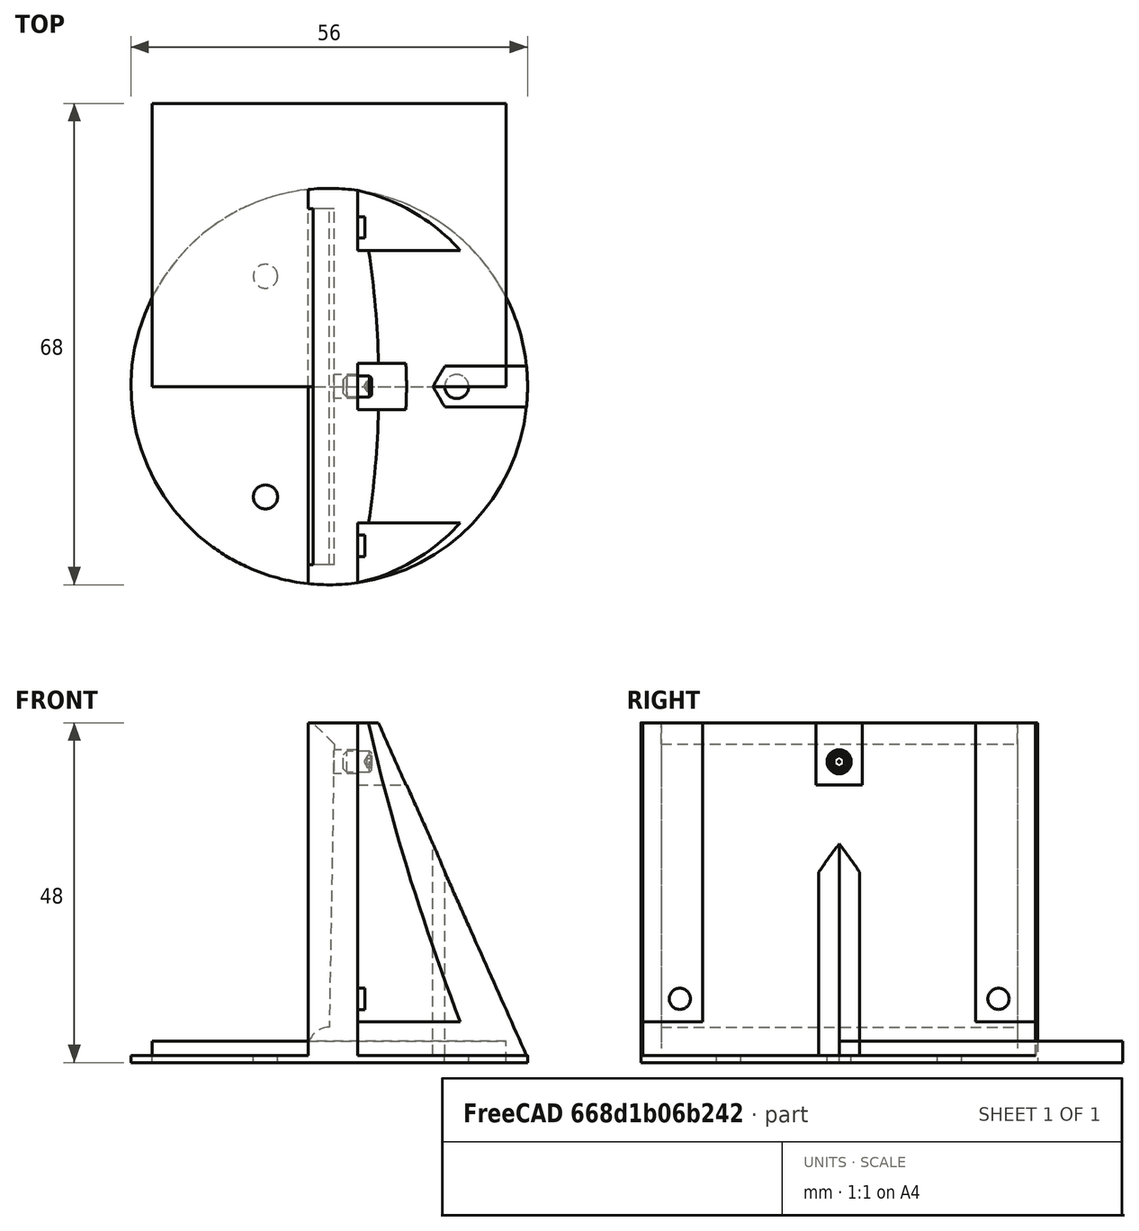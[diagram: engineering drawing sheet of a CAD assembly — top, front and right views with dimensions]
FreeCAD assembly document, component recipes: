
FREECAD ASSEMBLY — COMPONENT RECIPES ("IndexMirror")

This assembly document has 2 components, labeled P0..P1 below (a component is one placed body or linked part). 2 of them carry a construction recipe — the FreeCAD feature program that regenerates the part from scratch, quoted from this document or its linked companion documents; the rest are supplied as boundary geometry only. No exploded tour is included for this assembly.
COMPONENT P0 — recipe-attached ("IndexMirrorFrame", modeled in this document).
Construction recipe (the document's own serialized feature program — sketch geometry with constraints, then the solid features built on it; lengths are millimeters unless a unit is written):

FEATURE [PartDesign::Plane] DatumPlane  label="Plane_Base"
  AttachmentSupport = -> [XY_Plane001]
  Length = 60
  MapMode = 5
  ResizeMode = 0
  Width = 60
FEATURE [Sketcher::SketchObject] Sketch  label="Sketch_Base"
  ArcFitTolerance = 0
  AttachmentSupport = -> [DatumPlane]
  FullyConstrained = true
  MakeInternals = false
  MapMode = 5
  expr: Constraints[0] = <<Dimensions>>.index_mirror_base_diameter
  sketch-geometry (1):
    g0: Circle CenterX=0 CenterY=0 CenterZ=0 NormalX=0 NormalY=0 NormalZ=1 AngleXU=0 Radius=28
  constraints (2):
    c: Diameter(g0) = 56
    c: Coincident(g-1,g0)
FEATURE [PartDesign::Plane] DatumPlane001  label="Plane_BaseTop"
  AttachmentOffset = pos=(0,0,1) rot=(0,0,1;0rad)
  AttachmentSupport = -> [DatumPlane]
  Length = 60
  MapMode = 5
  Placement = pos=(0,0,1) rot=(0,0,1;0rad)
  ResizeMode = 0
  Width = 60
  expr: .AttachmentOffset.Base.z = <<Dimensions>>.index_mirror_base_thickness
FEATURE [PartDesign::Plane] DatumPlane002  label="Plane_MirrorBack"
  AttachmentSupport = -> [YZ_Plane002]
  Length = 60
  MapMode = 5
  Placement = pos=(0,0,0) rot=(0.57735,0.57735,0.57735;2.0944rad)
  ResizeMode = 0
  Width = 60
FEATURE [PartDesign::Plane] DatumPlane004  label="Plane_FrameFront"
  AttachmentOffset = pos=(0,0,-3) rot=(0,0,1;0rad)
  AttachmentSupport = -> [DatumPlane002]
  Length = 60
  MapMode = 5
  Placement = pos=(-3,0,0) rot=(0.57735,0.57735,0.57735;2.0944rad)
  ResizeMode = 0
  Width = 60
  expr: .AttachmentOffset.Base.z = -<<Dimensions>>.index_mirror_mirror_thickness
FEATURE [PartDesign::Plane] DatumPlane003  label="Plane_FrameBack"
  AttachmentOffset = pos=(0,0,7) rot=(0,0,1;0rad)
  AttachmentSupport = -> [DatumPlane004]
  Length = 60
  MapMode = 5
  Placement = pos=(4,0,0) rot=(0.57735,0.57735,0.57735;2.0944rad)
  ResizeMode = 0
  Width = 60
  expr: .AttachmentOffset.Base.z = <<Dimensions>>.mirror_frame_thickness
FEATURE [PartDesign::Plane] DatumPlane005  label="Plane_Top"
  AttachmentOffset = pos=(0,0,48) rot=(0,0,1;0rad)
  AttachmentSupport = -> [XY_Plane002]
  Length = 60
  MapMode = 5
  Placement = pos=(0,0,48) rot=(0,0,1;0rad)
  ResizeMode = 0
  Width = 60
  expr: .AttachmentOffset.Base.z = <<Dimensions>>.index_mirror_mirror_offset + <<Dimensions>>.index_mirror_mirror_height + <<Dimensions>>.mirror_frame_width
FEATURE [Sketcher::SketchObject] Sketch003
  ArcFitTolerance = 0
  AttachmentSupport = -> [DatumPlane001]
  FullyConstrained = true
  MakeInternals = false
  MapMode = 5
  Placement = pos=(0,0,1) rot=(0,0,1;0rad)
  expr: Constraints[4] = <<Dimensions>>.index_mirror_screw_diameter
  sketch-geometry (8):
    g0: Circle CenterX=-10.6066 CenterY=10.6066 CenterZ=0 NormalX=0 NormalY=0 NormalZ=1 AngleXU=0 Radius=1.5
    g1: Circle CenterX=-10.6066 CenterY=-10.6066 CenterZ=0 NormalX=0 NormalY=0 NormalZ=1 AngleXU=0 Radius=1.5
    g2: Circle CenterX=10.6066 CenterY=-10.6066 CenterZ=0 NormalX=0 NormalY=0 NormalZ=1 AngleXU=0 Radius=1.5
    g3: Circle CenterX=10.6066 CenterY=10.6066 CenterZ=0 NormalX=0 NormalY=0 NormalZ=1 AngleXU=0 Radius=1.5
    g4: LineSegment [constr] StartX=-10.6066 StartY=10.6066 StartZ=0 EndX=-10.6066 EndY=-10.6066 EndZ=0
    g5: LineSegment [constr] StartX=-10.6066 StartY=10.6066 StartZ=0 EndX=10.6066 EndY=10.6066 EndZ=0
    g6: LineSegment [constr] StartX=-10.6066 StartY=-10.6066 StartZ=0 EndX=10.6066 EndY=-10.6066 EndZ=0
    g7: LineSegment [constr] StartX=10.6066 StartY=10.6066 StartZ=0 EndX=10.6066 EndY=-10.6066 EndZ=0
  constraints (19):
    c: Equal(g0,g3)
    c: Equal(g1,g2)
    c: Equal(g0,g1)
    c: Distance(g0,g-1) = 15
    c: Diameter(g0) = 3
    c: Symmetric(g0,g2,g-1)
    c: Coincident(g4,g0)
    c: Coincident(g4,g1)
    c: Vertical(g4)
    c: Coincident(g5,g0)
    c: Coincident(g5,g3)
    c: Horizontal(g5)
    c: Coincident(g6,g1)
    c: Horizontal(g6)
    c: Coincident(g2,g6)
    c: Coincident(g7,g3)
    c: Coincident(g7,g2)
    c: Vertical(g7)
    c: Equal(g4,g6)
FEATURE [PartDesign::Line] HoleAxis_002  label="HoleAxis_1"
  AttacherType = Attacher::AttachEngineLine
  AttachmentOffset = pos=(0,0,1) rot=(0,0,1;0rad)
  AttachmentSupport = -> [Sketch003]
  Length = 4.2272
  MapMode = 19
  Placement = pos=(10.6066,10.6066,2) rot=(0,0,1;0rad)
  ResizeMode = 1
  expr: .AttachmentOffset.Base.z = <<Dimensions>>.index_mirror_base_thickness
FEATURE [PartDesign::Pad] Pad  label="Pad_Base"
  Direction = (0,0,1)
  Length = 10
  Length2 = 10
  Profile = -> Sketch
  ReferenceAxis = -> Sketch [N_Axis]
  Suppressed = false
  Type = 3
  UpToFace = -> DatumPlane001
FEATURE [Sketcher::SketchObject] Sketch010  label="Sketch_LoftBottom"
  ArcFitTolerance = 0
  AttachmentSupport = -> [DatumPlane001]
  ExternalGeometry = -> [Sketch,DatumPlane004]
  FullyConstrained = true
  MakeInternals = false
  MapMode = 5
  Placement = pos=(0,0,1) rot=(0,0,1;0rad)
  expr: Constraints[7] = <<Dimensions>>.mirror_frame_thickness
  sketch-geometry (4):
    g0: LineSegment StartX=-3 StartY=-27.8388 StartZ=0 EndX=-3 EndY=27.8388 EndZ=0
    g1: ArcOfCircle CenterX=0 CenterY=0 CenterZ=0 NormalX=0 NormalY=0 NormalZ=1 AngleXU=0 Radius=28 StartAngle=4.85574 EndAngle=7.71063
    g2: ArcOfCircle CenterX=0 CenterY=0 CenterZ=0 NormalX=0 NormalY=0 NormalZ=1 AngleXU=0 Radius=28 StartAngle=1.42745 EndAngle=1.67815
    g3: ArcOfCircle CenterX=0 CenterY=0 CenterZ=0 NormalX=0 NormalY=0 NormalZ=1 AngleXU=0 Radius=28 StartAngle=4.60504 EndAngle=4.85574
  constraints (12):
    c: PointOnObject(g0,g-4)
    c: Vertical(g0)
    c: Coincident(g2,g1)
    c: Coincident(g3,g1)
    c: Coincident(g3,g1)
    c: Coincident(g2,g1)
    c: Coincident(g2,g0)
    c: DistanceX(g0,g1) = 7
    c: Coincident(g3,g0)
    c: Coincident(g1,g-3)
    c: Equal(g1,g-3)
    c: Vertical(g1,g1)
FEATURE [Sketcher::SketchObject] Sketch011  label="Sketch_LoftTop"
  ArcFitTolerance = 0
  AttachmentSupport = -> [DatumPlane005]
  ExternalGeometry = -> [Sketch,DatumPlane004]
  FullyConstrained = true
  MakeInternals = false
  MapMode = 5
  Placement = pos=(0,0,48) rot=(0,0,1;0rad)
  expr: Constraints[11] = <<Dimensions>>.mirror_frame_thickness
  sketch-geometry (6):
    g0: LineSegment StartX=-3 StartY=27.8388 StartZ=0 EndX=-3 EndY=-27.8388 EndZ=0
    g1: LineSegment [constr] StartX=0 StartY=0 StartZ=0 EndX=-3 EndY=0 EndZ=0
    g2: ArcOfCircle CenterX=-122.5 CenterY=4.05e-14 CenterZ=0 NormalX=0 NormalY=0 NormalZ=1 AngleXU=0 Radius=129.5 StartAngle=6.06752 EndAngle=6.49885
    g3: ArcOfCircle CenterX=0 CenterY=0 CenterZ=0 NormalX=0 NormalY=0 NormalZ=1 AngleXU=0 Radius=28 StartAngle=1.42745 EndAngle=1.67815
    g4: ArcOfCircle CenterX=0 CenterY=0 CenterZ=0 NormalX=0 NormalY=0 NormalZ=1 AngleXU=0 Radius=28 StartAngle=4.60504 EndAngle=4.85574
    g5: GeomPoint [constr] X=7 Y=0 Z=0
  constraints (17):
    c: PointOnObject(g1,g0)
    c: Horizontal(g1)
    c: Symmetric(g0,g0,g1)
    c: PointOnObject(g0,g-4)
    c: Coincident(g-3,g1)
    c: Coincident(g3,g2)
    c: Coincident(g4,g2)
    c: Coincident(g3,g4)
    c: PointOnObject(g5,g2)
    c: Horizontal(g5,g1)
    c: DistanceX(g1,g5) = 10
    c: DistanceX(g0,g2) = 7
    c: Coincident(g0,g3)
    c: Coincident(g1,g3)
    c: Equal(g3,g-3)
    c: Vertical(g2,g2)
    c: Coincident(g0,g4)
FEATURE [PartDesign::AdditiveLoft] AdditiveLoft
  BaseFeature = -> Pad
  Closed = false
  Profile = -> Sketch010
  Ruled = false
  Sections = -> [Sketch011]
  Suppressed = false
FEATURE [Sketcher::SketchObject] Sketch012  label="Sketch_MirrorSlot"
  ArcFitTolerance = 0
  AttachmentSupport = -> [XZ_Plane002]
  ExternalGeometry = -> [DatumPlane002,DatumPlane004]
  FullyConstrained = true
  MakeInternals = false
  MapMode = 5
  Placement = pos=(0,0,0) rot=(1,0,0;1.5708rad)
  expr: Constraints[7] = <<Dimensions>>.index_mirror_mirror_offset
  expr: Constraints[8] = <<Dimensions>>.index_mirror_mirror_height
  sketch-geometry (4):
    g0: LineSegment StartX=0.698203 StartY=45 StartZ=0 EndX=-1e-15 EndY=5 EndZ=0
    g1: LineSegment StartX=0.698203 StartY=45 StartZ=0 EndX=-3 EndY=48.6982 EndZ=0
    g2: ArcOfCircle CenterX=-1e-15 CenterY=2 CenterZ=0 NormalX=0 NormalY=0 NormalZ=1 AngleXU=0 Radius=3 StartAngle=1.5708 EndAngle=3.14159
    g3: LineSegment StartX=-3 StartY=48.6982 StartZ=0 EndX=-3 EndY=2 EndZ=0
  constraints (13):
    c: Coincident(g1,g0)
    c: Coincident(g2,g0)
    c: Coincident(g3,g1)
    c: Coincident(g3,g2)
    c: PointOnObject(g2,g-4)
    c: Horizontal(g2,g2)
    c: Vertical(g2,g0)
    c: DistanceY(g-1,g0) = 5
    c: DistanceY(g0,g0) = 40
    c: Angle(g3,g1) = 0.785398
    c: PointOnObject(g0,g-3)
    c: PointOnObject(g1,g-4)
    c: Angle(g-3,g0) = 3.12414
FEATURE [PartDesign::Pocket] Pocket  label="Pocket_MirrorSlot"
  BaseFeature = -> AdditiveLoft
  Direction = (0,1,-2e-16)
  Length = 50.3
  Length2 = 5
  Midplane = true
  Profile = -> Sketch012
  ReferenceAxis = -> Sketch012 [N_Axis]
  Suppressed = false
  Type = 0
  expr: Length = <<Dimensions>>.index_mirror_mirror_width + 2 * <<Dimensions>>.clearance_tight_fit
FEATURE [Sketcher::SketchObject] Sketch013  label="Sketch_Screw"
  ArcFitTolerance = 0
  AttachmentSupport = -> [DatumPlane]
  ExternalGeometry = -> [Sketch]
  FullyConstrained = true
  MakeInternals = false
  MapMode = 5
  expr: Constraints[17] = <<Dimensions>>.index_mirror_screw_diameter
  expr: Constraints[18] = <<Dimensions>>.index_mirror_nut_S
  expr: Constraints[25] = <<Dimensions>>.index_mirror_screw_center_distance
  sketch-geometry (9):
    g0: Circle CenterX=-9 CenterY=15.5885 CenterZ=0 NormalX=0 NormalY=0 NormalZ=1 AngleXU=0 Radius=1.5
    g1: LineSegment [constr] StartX=-7.41229 StartY=12.8385 StartZ=0 EndX=-5.82457 EndY=15.5885 EndZ=0
    g2: LineSegment [constr] StartX=-5.82457 StartY=15.5885 StartZ=0 EndX=-7.41229 EndY=18.3385 EndZ=0
    g3: LineSegment [constr] StartX=-7.41229 StartY=18.3385 StartZ=0 EndX=-10.5877 EndY=18.3385 EndZ=0
    g4: LineSegment [constr] StartX=-10.5877 StartY=18.3385 StartZ=0 EndX=-12.1754 EndY=15.5885 EndZ=0
    g5: LineSegment [constr] StartX=-12.1754 StartY=15.5885 StartZ=0 EndX=-10.5877 EndY=12.8385 EndZ=0
    g6: LineSegment [constr] StartX=-10.5877 StartY=12.8385 StartZ=0 EndX=-7.41229 EndY=12.8385 EndZ=0
    g7: Circle [constr] CenterX=-9 CenterY=15.5885 CenterZ=0 NormalX=0 NormalY=0 NormalZ=1 AngleXU=0 Radius=3.17543
    g8: LineSegment [constr] StartX=-14 StartY=24.2487 StartZ=0 EndX=0 EndY=0 EndZ=0
  constraints (22):
    c: Coincident(g1,g2)
    c: Coincident(g2,g3)
    c: Coincident(g3,g4)
    c: Coincident(g4,g5)
    c: Coincident(g5,g6)
    c: Coincident(g6,g1)
    c: Equal(g1, g2-g6) x5
    c: PointOnObject(g1,g7)
    c: PointOnObject(g2,g7)
    c: PointOnObject(g4,g7)
    c: PointOnObject(g5,g7)
    c: PointOnObject(g6,g7)
    c: Coincident(g7,g0)
    c: Diameter(g0) = 3
    c: Distance(g3,g1) = 5.5
    c: Coincident(g8,g-3)
    c: Angle(g-1,g8) = 2.0944
    c: PointOnObject(g3,g7)
    c: PointOnObject(g8,g-3)
    c: PointOnObject(g1,g8)
    c: PointOnObject(g3,g8)
    c: Distance(g0,g8) = 18
FEATURE [PartDesign::Hole] Hole  label="Hole_Attachment"
  BaseFeature = -> Pocket
  CustomThreadClearance = 0
  Depth = 157.517
  DepthType = 1
  Diameter = 3.4
  DrillForDepth = false
  DrillPoint = 1
  DrillPointAngle = 118
  HoleCutCountersinkAngle = 90
  HoleCutCustomValues = false
  HoleCutDepth = 0
  HoleCutDiameter = 6.1
  HoleCutType = 0
  ModelThread = false
  Profile = -> Sketch013
  Reversed = true
  Suppressed = false
  Tapered = false
  TaperedAngle = 90
  ThreadClass = 0
  ThreadDepth = 157.517
  ThreadDepthType = 0
  ThreadDirection = 0
  ThreadFit = 0
  ThreadSize = 9
  ThreadType = 1
  Threaded = false
  UseCustomThreadClearance = false
  expr: ThreadSize = <<Dimensions>>.index_mirror_screw_type
FEATURE [Sketcher::SketchObject] Sketch014
  ArcFitTolerance = 0
  AttachmentSupport = -> [DatumPlane001]
  ExternalGeometry = -> [Sketch013,Sketch]
  FullyConstrained = true
  MakeInternals = false
  MapMode = 5
  Placement = pos=(0,0,1) rot=(0,0,1;0rad)
  expr: Constraints[18] = <<Dimensions>>.index_mirror_nut_S + 2 * <<Dimensions>>.clearance_tight_fit
  sketch-geometry (11):
    g0: ArcOfCircle CenterX=3.23676e-11 CenterY=1.36288e-11 CenterZ=0 NormalX=0 NormalY=0 NormalZ=1 AngleXU=0 Radius=28 StartAngle=1.99064 EndAngle=2.19815
    g1: LineSegment StartX=-7.32568 StartY=12.6885 StartZ=0 EndX=-5.65137 EndY=15.5885 EndZ=0
    g2: LineSegment StartX=-5.65137 StartY=15.5885 StartZ=0 EndX=-7.32568 EndY=18.4885 EndZ=0
    g3: LineSegment [constr] StartX=-7.32568 StartY=18.4885 StartZ=0 EndX=-10.6743 EndY=18.4885 EndZ=0
    g4: LineSegment [constr] StartX=-10.6743 StartY=18.4885 StartZ=0 EndX=-12.3486 EndY=15.5885 EndZ=0
    g5: LineSegment StartX=-12.3486 StartY=15.5885 StartZ=0 EndX=-10.6743 EndY=12.6885 EndZ=0
    g6: LineSegment StartX=-10.6743 StartY=12.6885 StartZ=0 EndX=-7.32568 EndY=12.6885 EndZ=0
    g7: Circle [constr] CenterX=-9 CenterY=15.5885 CenterZ=0 NormalX=0 NormalY=0 NormalZ=1 AngleXU=0 Radius=3.34863
    g8: LineSegment [constr] StartX=-14 StartY=24.2487 StartZ=0 EndX=0 EndY=0 EndZ=0
    g9: LineSegment StartX=-7.32568 StartY=18.4885 StartZ=0 EndX=-11.4132 EndY=25.5683 EndZ=0
    g10: LineSegment StartX=-12.3486 StartY=15.5885 StartZ=0 EndX=-16.4362 EndY=22.6683 EndZ=0
  constraints (28):
    c: Coincident(g1,g2)
    c: Coincident(g2,g3)
    c: Coincident(g3,g4)
    c: Coincident(g4,g5)
    c: Coincident(g5,g6)
    c: Coincident(g6,g1)
    c: Equal(g1, g2-g6) x5
    c: PointOnObject(g1,g7)
    c: PointOnObject(g2,g7)
    c: PointOnObject(g3,g7)
    c: PointOnObject(g4,g7)
    c: PointOnObject(g5,g7)
    c: PointOnObject(g6,g7)
    c: Coincident(g-3,g7)
    c: Distance(g5,g1) = 5.8
    c: PointOnObject(g8,g-4)
    c: Coincident(g8,g-4)
    c: PointOnObject(g3,g8)
    c: PointOnObject(g1,g8)
    c: Coincident(g9,g2)
    c: PointOnObject(g9,g-4)
    c: Coincident(g10,g5)
    c: PointOnObject(g10,g-4)
    c: Parallel(g10,g5)
    c: Parallel(g9,g2)
    c: Coincident(g0,g9)
    c: Coincident(g0,g10)
    c: Equal(g0,g-4)
FEATURE [PartDesign::Pocket] Pocket001
  BaseFeature = -> Hole
  Direction = (0,0,-1)
  Length = 5
  Length2 = 5
  Profile = -> Sketch014
  ReferenceAxis = -> Sketch014 [N_Axis]
  Reversed = true
  Suppressed = false
  Type = 1
FEATURE [PartDesign::PolarPattern] PolarPattern
  Angle = 360
  Axis = -> Sketch013 [N_Axis]
  BaseFeature = -> Pocket001
  Mode = 0
  Occurrences = 3
  Offset = 120
  Originals = -> [Hole,Pocket001]
  Refine = true
  Suppressed = false
  TransformMode = 0
FEATURE [Sketcher::SketchObject] Sketch015  label="Sketch_AdjustmentScrew"
  ArcFitTolerance = 0
  AttachmentSupport = -> [DatumPlane003]
  ExternalGeometry = -> [Sketch012]
  FullyConstrained = true
  MakeInternals = false
  MapMode = 5
  Placement = pos=(4,0,0) rot=(0.57735,0.57735,0.57735;2.0944rad)
  expr: Constraints[1] = <<Dimensions>>.mirror_adjustment_screw_diameter
  expr: Constraints[4] = <<Dimensions>>.mirror_clip_edge_distance
  sketch-geometry (2):
    g0: Circle CenterX=0 CenterY=42.5 CenterZ=0 NormalX=0 NormalY=0 NormalZ=1 AngleXU=0 Radius=1.5
    g1: GeomPoint [constr] X=0 Y=44 Z=0
  constraints (5):
    c: PointOnObject(g0,g-2)
    c: Diameter(g0) = 3
    c: PointOnObject(g1,g0)
    c: PointOnObject(g1,g-2)
    c: Distance(g-3,g1) = 1
FEATURE [PartDesign::Hole] Hole001  label="Hole_AdjustmentScrew"
  BaseFeature = -> PolarPattern
  CustomThreadClearance = 0
  Depth = 157.517
  DepthType = 1
  Diameter = 3.4
  DrillForDepth = false
  DrillPoint = 1
  DrillPointAngle = 118
  HoleCutCountersinkAngle = 90
  HoleCutCustomValues = false
  HoleCutDepth = 0
  HoleCutDiameter = 6.1
  HoleCutType = 0
  ModelThread = false
  Profile = -> Sketch015
  Suppressed = false
  Tapered = false
  TaperedAngle = 90
  ThreadClass = 0
  ThreadDepth = 157.517
  ThreadDepthType = 0
  ThreadDirection = 0
  ThreadFit = 0
  ThreadSize = 9
  ThreadType = 1
  Threaded = false
  UseCustomThreadClearance = false
  expr: ThreadSize = <<Dimensions>>.mirror_adjustment_screw_type
FEATURE [Sketcher::SketchObject] Sketch016  label="Sketch_ClipTop"
  ArcFitTolerance = 0
  AttachmentSupport = -> [DatumPlane003]
  ExternalGeometry = -> [Sketch015,DatumPlane005]
  FullyConstrained = true
  MakeInternals = false
  MapMode = 5
  Placement = pos=(4,0,0) rot=(0.57735,0.57735,0.57735;2.0944rad)
  expr: Constraints[10] = <<Dimensions>>.mirror_clip_width / 2 + <<Dimensions>>.clearance_loose_fit
  expr: Constraints[8] = <<Dimensions>>.mirror_clip_width + 2 * <<Dimensions>>.clearance_loose_fit
  sketch-geometry (4):
    g0: LineSegment StartX=-3.25 StartY=48 StartZ=0 EndX=-3.25 EndY=39.25 EndZ=0
    g1: LineSegment StartX=-3.25 StartY=39.25 StartZ=0 EndX=3.25 EndY=39.25 EndZ=0
    g2: LineSegment StartX=3.25 StartY=39.25 StartZ=0 EndX=3.25 EndY=48 EndZ=0
    g3: LineSegment StartX=-3.25 StartY=48 StartZ=0 EndX=3.25 EndY=48 EndZ=0
  constraints (11):
    c: Vertical(g0)
    c: Coincident(g1,g0)
    c: Coincident(g2,g1)
    c: PointOnObject(g0,g-4)
    c: PointOnObject(g2,g-4)
    c: Coincident(g3,g0)
    c: Coincident(g3,g2)
    c: Vertical(g2)
    c: DistanceX(g3,g3) = 6.5
    c: Symmetric(g1,g0,g-2)
    c: DistanceY(g1,g-3) = 3.25
FEATURE [PartDesign::Pocket] Pocket002  label="Pocket_ClipTop"
  BaseFeature = -> Hole001
  Direction = (-1,0,0)
  Length = 5
  Length2 = 5
  Profile = -> Sketch016
  ReferenceAxis = -> Sketch016 [N_Axis]
  Reversed = true
  Suppressed = false
  Type = 1
FEATURE [Sketcher::SketchObject] Sketch017  label="Sketch_ClipNotchSide"
  ArcFitTolerance = 0
  AttachmentSupport = -> [DatumPlane003]
  ExternalGeometry = -> [Sketch012]
  FullyConstrained = true
  MakeInternals = false
  MapMode = 5
  Placement = pos=(4,0,0) rot=(0.57735,0.57735,0.57735;2.0944rad)
  expr: Constraints[0] = <<Dimensions>>.mirror_adjustment_screw_diameter
  expr: Constraints[3] = <<Dimensions>>.mirror_clip_edge_distance + <<Dimensions>>.mirror_clip_width / 2
  expr: Constraints[4] = <<Dimensions>>.index_mirror_mirror_width / 2 - <<Dimensions>>.mirror_adjustment_screw_diameter / 2 - <<Dimensions>>.mirror_clip_edge_distance
  sketch-geometry (2):
    g0: Circle CenterX=-22.5 CenterY=9 CenterZ=0 NormalX=0 NormalY=0 NormalZ=1 AngleXU=0 Radius=1.5
    g1: Circle CenterX=22.5 CenterY=9 CenterZ=0 NormalX=0 NormalY=0 NormalZ=1 AngleXU=0 Radius=1.5
  constraints (5):
    c: Diameter(g0) = 3
    c: Equal(g0,g1)
    c: Symmetric(g0,g1,g-2)
    c: DistanceY(g-3,g0) = 4
    c: DistanceX(g0,g-3) = 22.5
FEATURE [Sketcher::SketchObject] Sketch018
  ArcFitTolerance = 0
  AttachmentSupport = -> [DatumPlane003]
  ExternalGeometry = -> [Sketch017,Sketch,DatumPlane005]
  FullyConstrained = true
  MakeInternals = false
  MapMode = 5
  Placement = pos=(4,0,0) rot=(0.57735,0.57735,0.57735;2.0944rad)
  expr: Constraints[20] = <<Dimensions>>.mirror_clip_width / 2 + <<Dimensions>>.clearance_loose_fit
  expr: Constraints[24] = <<Dimensions>>.mirror_clip_width / 2 + <<Dimensions>>.clearance_loose_fit
  sketch-geometry (9):
    g0: LineSegment StartX=-19.25 StartY=48 StartZ=0 EndX=-19.25 EndY=5.75 EndZ=0
    g1: LineSegment StartX=-19.25 StartY=5.75 StartZ=0 EndX=-28 EndY=5.75 EndZ=0
    g2: LineSegment StartX=-28 StartY=48 StartZ=0 EndX=-28 EndY=5.75 EndZ=0
    g3: LineSegment [constr] StartX=-28 StartY=9 StartZ=0 EndX=-19.25 EndY=9 EndZ=0
    g4: LineSegment StartX=28 StartY=48 StartZ=0 EndX=28 EndY=5.75 EndZ=0
    g5: LineSegment StartX=28 StartY=48 StartZ=0 EndX=19.25 EndY=48 EndZ=0
    g6: LineSegment StartX=19.25 StartY=48 StartZ=0 EndX=19.25 EndY=5.75 EndZ=0
    g7: LineSegment StartX=19.25 StartY=5.75 StartZ=0 EndX=28 EndY=5.75 EndZ=0
    g8: LineSegment StartX=-28 StartY=48 StartZ=0 EndX=-19.25 EndY=48 EndZ=0
  constraints (27):
    c: Coincident(g1,g0)
    c: Coincident(g2,g1)
    c: Vertical(g1,g-5)
    c: Vertical(g2)
    c: Horizontal(g1)
    c: PointOnObject(g3,g2)
    c: PointOnObject(g3,g0)
    c: Horizontal(g3)
    c: PointOnObject(g-3,g3)
    c: Horizontal(g5)
    c: Coincident(g6,g5)
    c: Coincident(g4,g5)
    c: Vertical(g4)
    c: Coincident(g7,g6)
    c: Coincident(g7,g4)
    c: Horizontal(g7)
    c: Vertical(g6)
    c: Symmetric(g0,g6,g-2)
    c: Equal(g2,g4)
    c: Equal(g1,g7)
    c: DistanceY(g1,g3) = 3.25
    c: PointOnObject(g2,g-6)
    c: Coincident(g8,g2)
    c: PointOnObject(g8,g-6)
    c: DistanceX(g-3,g3) = 3.25
    c: Vertical(g0)
    c: Coincident(g0,g8)
FEATURE [PartDesign::Pocket] Pocket003
  BaseFeature = -> Pocket002
  Direction = (-1,0,0)
  Length = 5
  Length2 = 5
  Profile = -> Sketch018
  ReferenceAxis = -> Sketch018 [N_Axis]
  Reversed = true
  Suppressed = false
  Type = 1
FEATURE [PartDesign::Pad] Pad003
  BaseFeature = -> Pocket003
  Direction = (1,0,0)
  Length = 1
  Length2 = 10
  Profile = -> Sketch017
  ReferenceAxis = -> Sketch017 [N_Axis]
  Suppressed = false
  Type = 0
FEATURE [PartDesign::Body] Body  label="IndexMirrorFrameBody"
  AllowCompound = false
  Group = -> [DatumPlane,DatumPlane001,DatumPlane002,DatumPlane003,DatumPlane004,DatumPlane005,Sketch,Sketch003,HoleAxis_002,Pad,Sketch010,Sketch011,AdditiveLoft,Sketch012,Pocket,Sketch013,Hole,Sketch014,Pocket001,PolarPattern,Sketch015,Hole001,Sketch016,Pocket002,Sketch017,Sketch018,Pocket003,Pad003]
  Origin = -> Origin002
  Tip = -> Pad003
COMPONENT P1 — recipe-attached ("Mirror", modeled in this document).
Construction recipe (the document's own serialized feature program — sketch geometry with constraints, then the solid features built on it; lengths are millimeters unless a unit is written):

FEATURE [Sketcher::SketchObject] Sketch002
  ArcFitTolerance = 0
  AttachmentSupport = -> [XY_Plane004]
  FullyConstrained = true
  MakeInternals = false
  MapMode = 2
  expr: Constraints[4] = <<Dimensions>>.index_mirror_mirror_height
  expr: Constraints[8] = <<Dimensions>>.index_mirror_mirror_width
  sketch-geometry (4):
    g0: LineSegment StartX=25 StartY=0 StartZ=0 EndX=25 EndY=40 EndZ=0
    g1: LineSegment StartX=25 StartY=40 StartZ=0 EndX=-25 EndY=40 EndZ=0
    g2: LineSegment StartX=-25 StartY=40 StartZ=0 EndX=-25 EndY=0 EndZ=0
    g3: LineSegment StartX=-25 StartY=0 StartZ=0 EndX=25 EndY=0 EndZ=0
  constraints (11):
    c: Coincident(g0,g1)
    c: Coincident(g1,g2)
    c: Coincident(g2,g3)
    c: Coincident(g3,g0)
    c: Distance(g2) = 40
    c: Vertical(g0)
    c: Horizontal(g3)
    c: Horizontal(g1)
    c: Distance(g1) = 50
    c: Vertical(g2)
    c: Symmetric(g2,g0,g-1)
FEATURE [PartDesign::Pad] Pad002
  Direction = (0,0,1)
  Length = 3
  Length2 = 10
  Profile = -> Sketch002
  ReferenceAxis = -> Sketch002 [N_Axis]
  Suppressed = false
  Type = 0
  expr: Length = <<Dimensions>>.index_mirror_mirror_thickness
FEATURE [PartDesign::Body] Body001
  AllowCompound = false
  Group = -> [Sketch002,Pad002]
  Origin = -> Origin004
  Tip = -> Pad002
PROVENANCE & LICENSES
A FreeCAD (.FCStd) document from a public repository crawl; recipes are the document's own serialized feature recipes (and, for linked parts, companion documents' recipes).
License: gpl-3.0.
